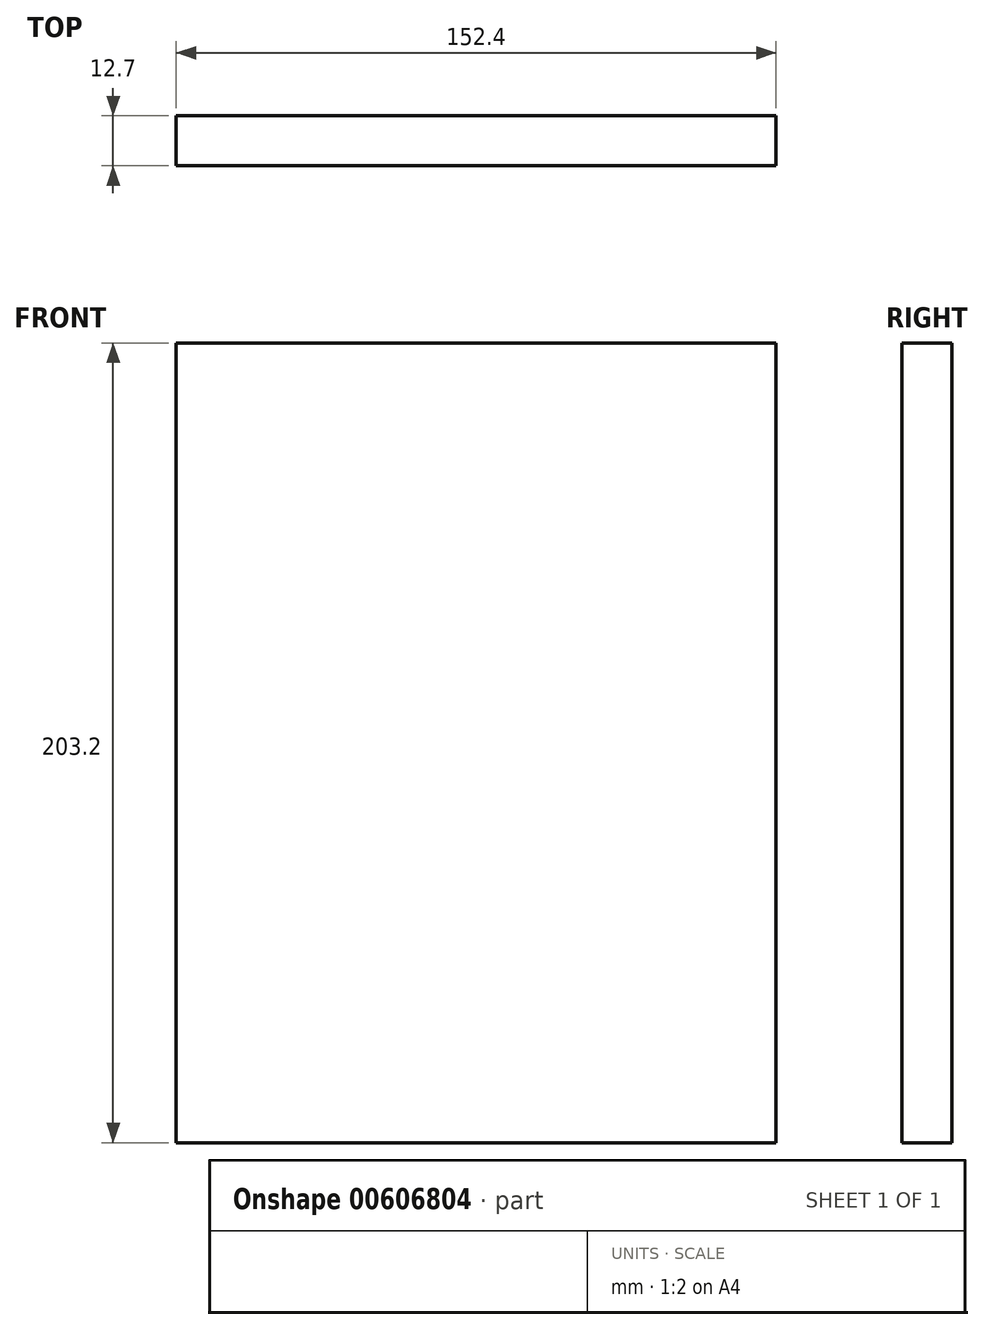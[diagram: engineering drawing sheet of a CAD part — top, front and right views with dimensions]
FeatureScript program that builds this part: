
annotation { "Feature Type Name" : "Feature", "Feature Type Description" : "" }
export const myFeature = defineFeature(function(context is Context, id is Id, definition is map)
    precondition{}
    {
        {
            var Q0;
            Q0=qCreatedBy(makeId("Front.planeOp"),FACE);
            var sketch = newSketch(context, id + "F0", { "sketchPlane" : qUnion([Q0])});
            skLineSegment(sketch, "E0.bottom", {"start": v(-104.15, 99.33) * mm, "end": v(48.25, 99.33) * mm});
            skLineSegment(sketch, "E0.top", {"start": v(-104.15, -103.87) * mm, "end": v(48.25, -103.87) * mm});
            skLineSegment(sketch, "E0.left", {"start": v(-104.15, 99.33) * mm, "end": v(-104.15, -103.87) * mm});
            skLineSegment(sketch, "E0.right", {"start": v(48.25, 99.33) * mm, "end": v(48.25, -103.87) * mm});
            skSolve(sketch);
        }
        {
            var Q0;
            Q0 = qSketchRegion(id + "F0", true);
            extrude(context, id + "F1", {"entities" : qUnion([Q0]), "depth" : 12.7 * mm, "offsetDistance" : 25.4 * mm});
        }
    });
